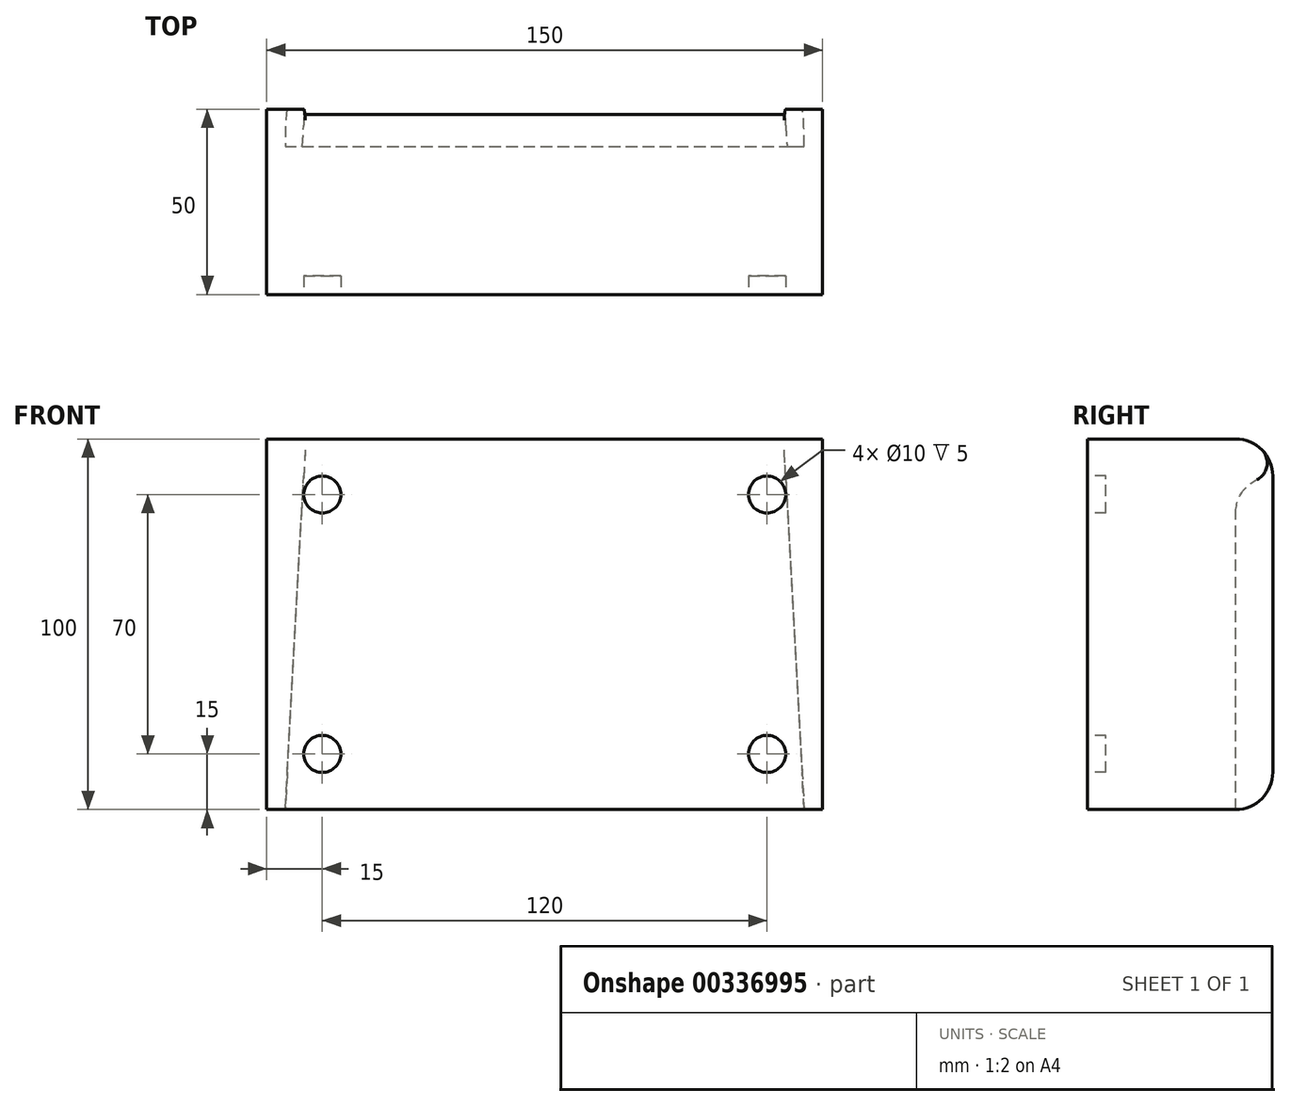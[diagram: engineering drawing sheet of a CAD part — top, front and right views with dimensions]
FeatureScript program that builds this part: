
annotation { "Feature Type Name" : "Feature", "Feature Type Description" : "" }
export const myFeature = defineFeature(function(context is Context, id is Id, definition is map)
    precondition{}
    {
        {
            var Q0;
            Q0=qCreatedBy(makeId("Top.planeOp"),FACE);
            var sketch = newSketch(context, id + "F0", { "sketchPlane" : qUnion([Q0])});
            skLineSegment(sketch, "E0.bottom", {"start": v(0, 0) * mm, "end": v(150, 0) * mm});
            skLineSegment(sketch, "E0.top", {"start": v(0, 50) * mm, "end": v(150, 50) * mm});
            skLineSegment(sketch, "E0.left", {"start": v(0, 0) * mm, "end": v(0, 50) * mm});
            skLineSegment(sketch, "E0.right", {"start": v(150, 0) * mm, "end": v(150, 50) * mm});
            skSolve(sketch);
        }
        {
            var Q0;
            Q0=makeQuery(id+"F0.imprint","IMPRINT",FACE,{"disambiguationData":[TD([[makeQuery(id+"F0.imprint","IMPRINT",EDGE,{"derivedFrom":sQuery(id+"F0.wireOp",EDGE,"E0.bottom")}),1.0]])]});
            extrude(context, id + "F1", {"entities" : qUnion([Q0]), "depth" : 100 * mm});
        }
        {
            var Q0;
            Q0=makeQuery(id+"F1.opExtrude","SWEPT_FACE",FACE,{"disambiguationData":[OSD([sQuery(id+"F0.wireOp",EDGE,"E0.top")])]});
            var sketch = newSketch(context, id + "F2", { "sketchPlane" : qUnion([Q0])});
            skLineSegment(sketch, "E1", {"start": v(-145, 0) * mm, "end": v(-5, 0) * mm});
            skLineSegment(sketch, "E2", {"start": v(-5, 0) * mm, "end": v(-10, 90) * mm});
            skLineSegment(sketch, "E3", {"start": v(-10, 90) * mm, "end": v(-140, 90) * mm});
            skLineSegment(sketch, "E4", {"start": v(-140, 90) * mm, "end": v(-145, 0) * mm});
            skSolve(sketch);
        }
        {
            var Q0;
            Q0=makeQuery(id+"F2.imprint","IMPRINT",FACE,{"disambiguationData":[TD([[makeQuery(id+"F2.imprint","IMPRINT",EDGE,{"derivedFrom":sQuery(id+"F2.wireOp",EDGE,"E1")}),-1.0]])]});
            extrude(context, id + "F3", {"entities" : qUnion([Q0]), "operationType" : NewBodyOperationType.REMOVE, "oppositeDirection" : true, "depth" : 10 * mm});
        }
        {
            var Q0;
            Q0=makeQuery(id+"F1.opExtrude","SWEPT_FACE",FACE,{"disambiguationData":[OSD([sQuery(id+"F0.wireOp",EDGE,"E0.bottom")])]});
            var sketch = newSketch(context, id + "F4", { "sketchPlane" : qUnion([Q0])});
            skCircle(sketch, "E5", {"center": v(15, 85) * mm, "radius": 5 * mm});
            skCircle(sketch, "E6", {"center": v(135, 85) * mm, "radius": 5 * mm});
            skCircle(sketch, "E7", {"center": v(135, 15) * mm, "radius": 5 * mm});
            skCircle(sketch, "E8", {"center": v(15, 15) * mm, "radius": 5 * mm});
            skSolve(sketch);
        }
        {
            var Q0;
            Q0 = qSketchRegion(id + "F4", true);
            extrude(context, id + "F5", {"entities" : qUnion([Q0]), "operationType" : NewBodyOperationType.REMOVE, "oppositeDirection" : true, "depth" : 5 * mm});
        }
        {
            var Q0;
            Q0=makeQuery(id+"F3.boolean.opBoolean","COPY",EDGE,{"derivedFrom":makeQuery(id+"F3.opExtrude","CAP_EDGE",EDGE,{"disambiguationData":[OSD([sQuery(id+"F2.wireOp",EDGE,"E3")])],"isStart":false})});
            fillet(context, id + "F6", {"entities" : qUnion([Q0]), "radius" : 10 * mm, "tangentPropagation" : true, "allowEdgeOverflow" : false});
        }
        {
            var Q0;
            {var subQ0=sQuery(id+"F0.wireOp",EDGE,"E0.right");var subQ1=sQuery(id+"F0.wireOp",EDGE,"E0.top");Q0=makeQuery(id+"F3.boolean.opBoolean","SPLIT",EDGE,{"disambiguationData":[TD([makeQuery(id+"F1.opExtrude","SWEPT_FACE",FACE,{"disambiguationData":[OSD([subQ0])]})])],"derivedFrom":makeQuery(id+"F1.opExtrude","CAP_EDGE",EDGE,{"disambiguationData":[OSD([subQ1])],"isStart":true})});}
            var Q1;
            {var subQ0=sQuery(id+"F0.wireOp",EDGE,"E0.left");var subQ1=sQuery(id+"F0.wireOp",EDGE,"E0.top");Q1=makeQuery(id+"F3.boolean.opBoolean","SPLIT",EDGE,{"disambiguationData":[TD([makeQuery(id+"F1.opExtrude","SWEPT_FACE",FACE,{"disambiguationData":[OSD([subQ0])]})])],"derivedFrom":makeQuery(id+"F1.opExtrude","CAP_EDGE",EDGE,{"disambiguationData":[OSD([subQ1])],"isStart":true})});}
            var Q2;
            Q2=makeQuery(id+"F1.opExtrude","CAP_EDGE",EDGE,{"disambiguationData":[OSD([sQuery(id+"F0.wireOp",EDGE,"E0.top")])],"isStart":false});
            fillet(context, id + "F7", {"entities" : qUnion([Q0, Q1, Q2]), "radius" : 10 * mm, "tangentPropagation" : true, "allowEdgeOverflow" : false});
        }
        {
            var Q0;
            Q0=makeQuery(id+"F7.opFillet","BLEND_EDGE",EDGE,{"blendedFrom":[makeQuery(id+"F1.opExtrude","CAP_EDGE",EDGE,{"disambiguationData":[OSD([sQuery(id+"F0.wireOp",EDGE,"E0.top")])],"isStart":false}),makeQuery(id+"F6.opFillet","BLEND_FACE",FACE,{"disambiguationData":[OSD([sQuery(id+"F2.wireOp",EDGE,"E3")])]})],"blendedInto":[makeQuery(id+"F6.opFillet","BLEND_FACE",FACE,{"disambiguationData":[OSD([sQuery(id+"F2.wireOp",EDGE,"E3")])]})]});
            fillet(context, id + "F8", {"entities" : qUnion([Q0]), "radius" : 5 * mm, "tangentPropagation" : true, "allowEdgeOverflow" : false});
        }
    });
